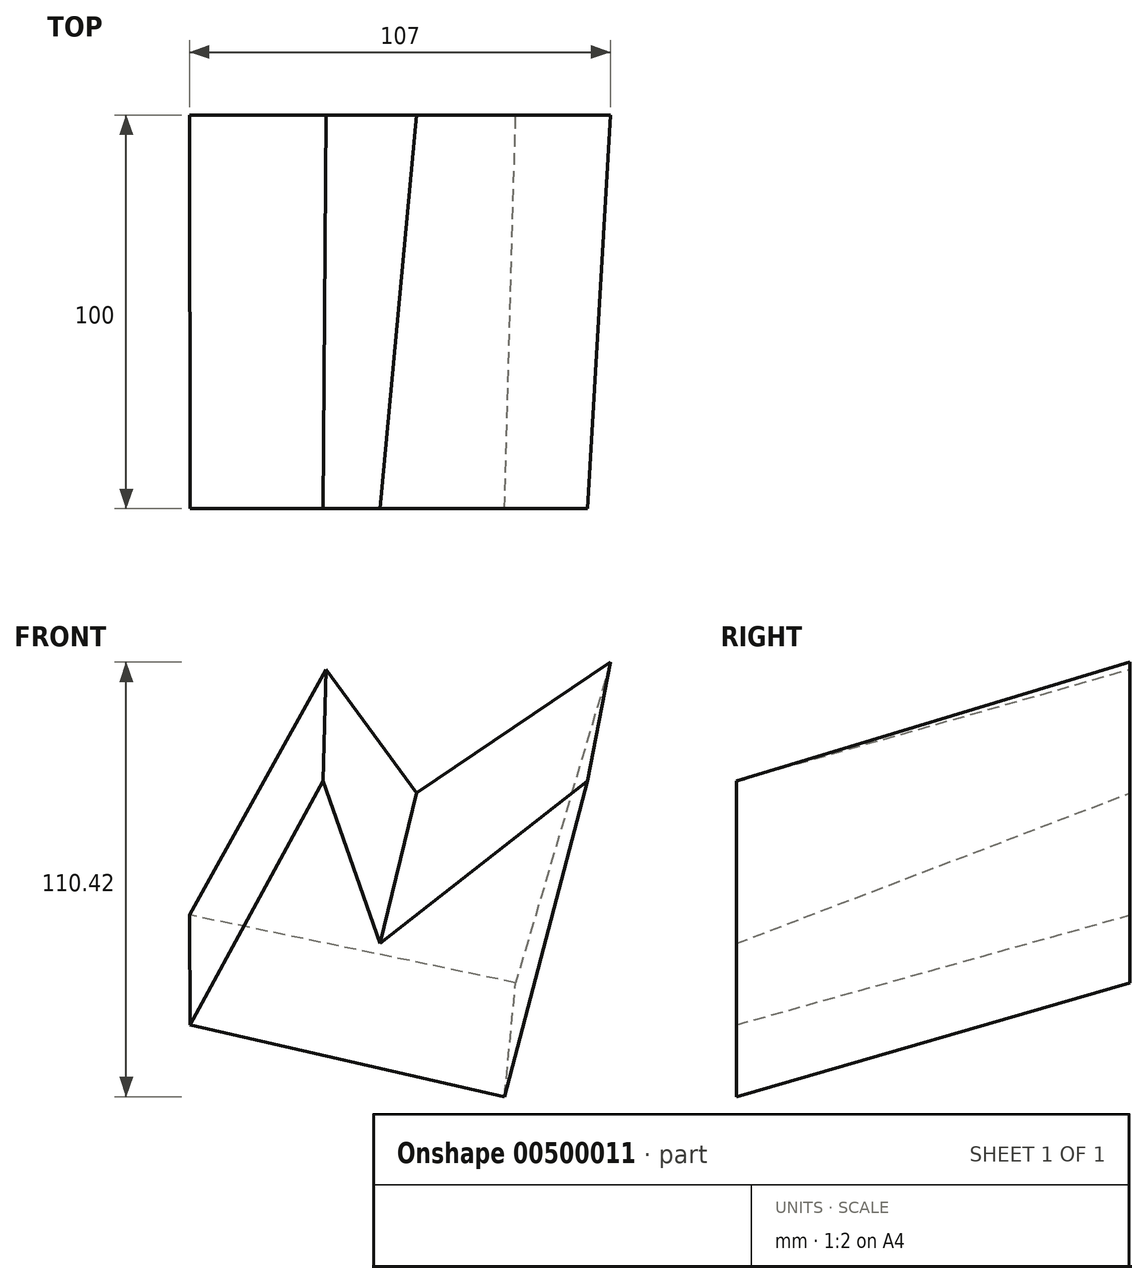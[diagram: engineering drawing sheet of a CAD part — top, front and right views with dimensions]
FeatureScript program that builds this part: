
annotation { "Feature Type Name" : "Feature", "Feature Type Description" : "" }
export const myFeature = defineFeature(function(context is Context, id is Id, definition is map)
    precondition{}
    {
        {
            var Q0;
            Q0=qCreatedBy(makeId("Front.planeOp"),FACE);
            var sketch = newSketch(context, id + "F0", { "sketchPlane" : qUnion([Q0])});
            skLineSegment(sketch, "E0", {"start": v(-22.66, 45.18) * mm, "end": v(-57.66, -17.64) * mm});
            skLineSegment(sketch, "E1", {"start": v(-22.95, 44.9) * mm, "end": v(0, 13.34) * mm});
            skLineSegment(sketch, "E2", {"start": v(0, 13.34) * mm, "end": v(49.34, 46.62) * mm});
            skLineSegment(sketch, "E3", {"start": v(49.34, 46.62) * mm, "end": v(25.25, -34.86) * mm});
            skLineSegment(sketch, "E4", {"start": v(25.25, -34.86) * mm, "end": v(-57.66, -17.64) * mm});
            skSolve(sketch);
        }
        {
            var Q0;
            Q0=qCreatedBy(makeId("Front.planeOp"),FACE);
            cPlane(context, id + "F1", {"entities" : qUnion([Q0]), "cplaneType" : CPlaneType.OFFSET, "offset" : 100 * mm, "width" : 150 * mm, "height" : 150 * mm});
        }
        {
            var Q0;
            Q0=qCreatedBy(id+"F1.planeOp",FACE);
            var sketch = newSketch(context, id + "F2", { "sketchPlane" : qUnion([Q0])});
            skLineSegment(sketch, "E5", {"start": v(-23.75, 16.4) * mm, "end": v(-57.42, -45.53) * mm});
            skLineSegment(sketch, "E6", {"start": v(-23.75, 16.4) * mm, "end": v(-9.21, -24.87) * mm});
            skLineSegment(sketch, "E7", {"start": v(-9.21, -24.87) * mm, "end": v(43.6, 16.4) * mm});
            skLineSegment(sketch, "E8", {"start": v(43.6, 16.54) * mm, "end": v(22.42, -63.8) * mm});
            skLineSegment(sketch, "E9", {"start": v(-57.42, -45.53) * mm, "end": v(22.42, -63.8) * mm});
            skSolve(sketch);
        }
        {
            var Q0;
            Q0=makeQuery(id+"F2.imprint","IMPRINT",FACE,{"disambiguationData":[TD([[makeQuery(id+"F2.imprint","IMPRINT",EDGE,{"derivedFrom":sQuery(id+"F2.wireOp",EDGE,"E5")}),1.0]])]});
            var Q1;
            {var subQ0=sQuery(id+"F0.wireOp",EDGE,"E2");Q1=makeQuery(id+"F0.imprint","IMPRINT",FACE,{"disambiguationData":[TD([[makeQuery(id+"F0.imprint","IMPRINT",EDGE,{"derivedFrom":subQ0}),-1.0]])]});}
            loft(context, id + "F3", {"sheetProfilesArray" : [{ "sheetProfileEntities" : qUnion([Q0]) }, { "sheetProfileEntities" : qUnion([Q1]) }]});
        }
    });
